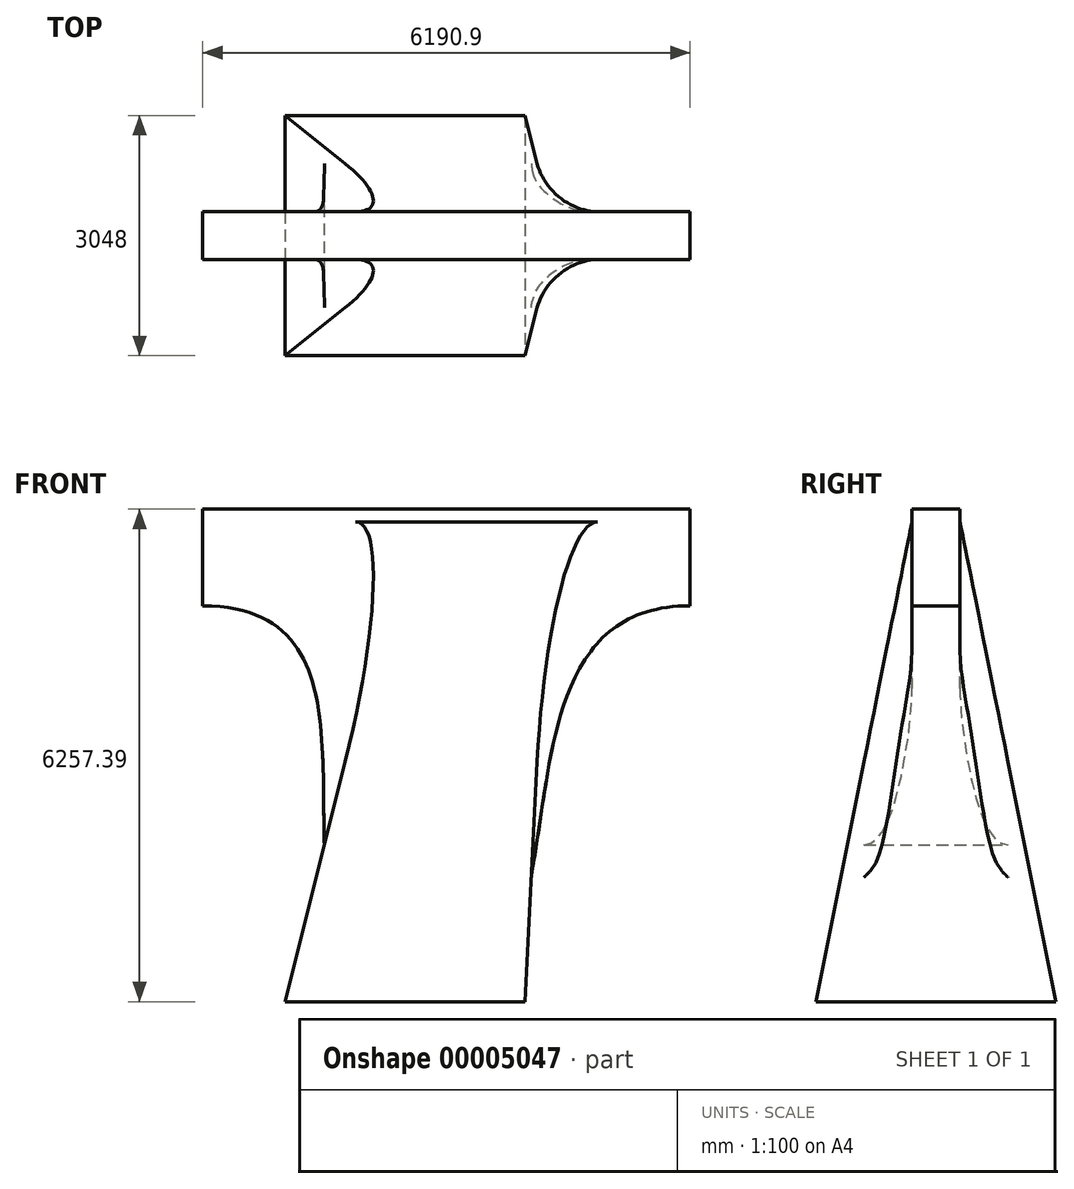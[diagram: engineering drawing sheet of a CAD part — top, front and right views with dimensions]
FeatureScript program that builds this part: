
annotation { "Feature Type Name" : "Feature", "Feature Type Description" : "" }
export const myFeature = defineFeature(function(context is Context, id is Id, definition is map)
    precondition{}
    {
        {
            var Q0;
            Q0=qCreatedBy(makeId("Top.planeOp"),FACE);
            cPlane(context, id + "F0", {"entities" : qUnion([Q0]), "cplaneType" : CPlaneType.OFFSET, "offset" : 6096 * mm, "width" : 152.4 * mm, "height" : 152.4 * mm});
        }
        {
            var Q0;
            Q0=qCreatedBy(makeId("Top.planeOp"),FACE);
            var sketch = newSketch(context, id + "F1", { "sketchPlane" : qUnion([Q0])});
            skLineSegment(sketch, "E0.bottom", {"start": v(-6096, 1524) * mm, "end": v(-3048, 1524) * mm});
            skLineSegment(sketch, "E0.top", {"start": v(-6096, -1524) * mm, "end": v(-3048, -1524) * mm});
            skLineSegment(sketch, "E0.left", {"start": v(-6096, 1524) * mm, "end": v(-6096, -1524) * mm});
            skLineSegment(sketch, "E0.right", {"start": v(-3048, 1524) * mm, "end": v(-3048, -1524) * mm});
            skSolve(sketch);
        }
        {
            var Q0;
            Q0=qCreatedBy(id+"F0.planeOp",FACE);
            var sketch = newSketch(context, id + "F2", { "sketchPlane" : qUnion([Q0])});
            skLineSegment(sketch, "E1.bottom", {"start": v(-4572, 304.8) * mm, "end": v(-2743.2, 304.8) * mm});
            skLineSegment(sketch, "E1.top", {"start": v(-4572, -304.8) * mm, "end": v(-2743.2, -304.8) * mm});
            skLineSegment(sketch, "E1.left", {"start": v(-4572, 304.8) * mm, "end": v(-4572, -304.8) * mm});
            skLineSegment(sketch, "E1.right", {"start": v(-2743.2, 304.8) * mm, "end": v(-2743.2, -304.8) * mm});
            skSolve(sketch);
        }
        {
            var Q0;
            Q0=makeQuery(id+"F1.imprint","IMPRINT",FACE,{"disambiguationData":[TD([[makeQuery(id+"F1.imprint","IMPRINT",EDGE,{"derivedFrom":sQuery(id+"F1.wireOp",EDGE,"E0.bottom")}),-1.0]])]});
            var Q1;
            Q1=makeQuery(id+"F2.imprint","IMPRINT",FACE,{"disambiguationData":[TD([[makeQuery(id+"F2.imprint","IMPRINT",EDGE,{"derivedFrom":sQuery(id+"F2.wireOp",EDGE,"E1.bottom")}),-1.0]])]});
            var Q2;
            Q2=sQuery(id+"F1.wireOp",VERTEX,"E0.right.end");
            var Q3;
            Q3=sQuery(id+"F2.wireOp",VERTEX,"E1.bottom.end");
            loft(context, id + "F3", {"sheetProfilesArray" : [{ "sheetProfileEntities" : qUnion([Q0]) }, { "sheetProfileEntities" : qUnion([Q1]) }], "connections" : [{ "connectionEntities" : qUnion([Q2, Q3]), "connectionEdgeQueries" : qUnion([]), "connectionEdgeParameters" : [] }]});
        }
        {
            var Q0;
            Q0=qCreatedBy(makeId("Front.planeOp"),FACE);
            var sketch = newSketch(context, id + "F4", { "sketchPlane" : qUnion([Q0])});
            skLineSegment(sketch, "E2", {"start": v(-7144.62, 6257.4) * mm, "end": v(-7144.62, 5029) * mm});
            skLineSegment(sketch, "E3", {"start": v(-7144.62, 6257.4) * mm, "end": v(-953.72, 6257.4) * mm});
            skLineSegment(sketch, "E4", {"start": v(-953.72, 6257.4) * mm, "end": v(-953.72, 5029) * mm});
            skFitSpline(sketch, "E5", {"points": [v(-953.72, 5029) * mm, v(-4320.53, 35.81) * mm], "startDerivative": vector(-8592.9, 0) * mm, "endDerivative": vector(-7049.9, 355.53) * mm});
            skFitSpline(sketch, "E6", {"points": [v(-7144.62, 5029) * mm, v(-4320.53, 35.81) * mm], "startDerivative": vector(8814.65, 0) * mm, "endDerivative": vector(7823.2, -629.46) * mm});
            skSolve(sketch);
        }
        {
            var Q0;
            Q0 = qSketchRegion(id + "F4", true);
            extrude(context, id + "F5", {"entities" : qUnion([Q0]), "operationType" : NewBodyOperationType.ADD, "endBound" : BoundingType.SYMMETRIC, "depth" : 609.6 * mm});
        }
        {
            var Q0;
            Q0=makeQuery(id+"F5.boolean.opBoolean","INTERSECT",EDGE,{"derivedFrom":[makeQuery(id+"F3.opLoft","SWEPT_FACE",FACE,{"disambiguationData":[OSD([sQuery(id+"F1.wireOp",EDGE,"E0.bottom"),sQuery(id+"F1.wireOp",EDGE,"E0.top"),sQuery(id+"F1.wireOp",EDGE,"E0.left"),sQuery(id+"F2.wireOp",EDGE,"E1.bottom"),sQuery(id+"F2.wireOp",EDGE,"E1.top"),sQuery(id+"F2.wireOp",EDGE,"E1.left")])]}),makeQuery(id+"F5.opExtrude","SWEPT_FACE",FACE,{"disambiguationData":[OSD([sQuery(id+"F4.wireOp",EDGE,"8ee350d9-5123-4934-8b01-f55df6ba07b4")])]})]});
            var Q1;
            Q1=makeQuery(id+"F5.boolean.opBoolean","INTERSECT",EDGE,{"derivedFrom":[makeQuery(id+"F3.opLoft","SWEPT_FACE",FACE,{"disambiguationData":[OSD([sQuery(id+"F1.wireOp",EDGE,"E0.bottom"),sQuery(id+"F1.wireOp",EDGE,"E0.top"),sQuery(id+"F1.wireOp",EDGE,"E0.left"),sQuery(id+"F2.wireOp",EDGE,"E1.bottom"),sQuery(id+"F2.wireOp",EDGE,"E1.top"),sQuery(id+"F2.wireOp",EDGE,"E1.left")])]}),makeQuery(id+"F5.opExtrude","CAP_FACE",FACE,{"disambiguationData":[OSD([sQuery(id+"F4.wireOp",EDGE,"E2"),sQuery(id+"F4.wireOp",EDGE,"E3"),sQuery(id+"F4.wireOp",EDGE,"E4"),sQuery(id+"F4.wireOp",EDGE,"E5"),sQuery(id+"F4.wireOp",EDGE,"8ee350d9-5123-4934-8b01-f55df6ba07b4")])],"isStart":false})]});
            var Q2;
            Q2=makeQuery(id+"F5.boolean.opBoolean","INTERSECT",EDGE,{"derivedFrom":[makeQuery(id+"F3.opLoft","SWEPT_FACE",FACE,{"disambiguationData":[OSD([sQuery(id+"F1.wireOp",EDGE,"E0.bottom"),sQuery(id+"F1.wireOp",EDGE,"E0.top"),sQuery(id+"F1.wireOp",EDGE,"E0.left"),sQuery(id+"F2.wireOp",EDGE,"E1.bottom"),sQuery(id+"F2.wireOp",EDGE,"E1.top"),sQuery(id+"F2.wireOp",EDGE,"E1.left")])]}),makeQuery(id+"F5.opExtrude","CAP_FACE",FACE,{"disambiguationData":[OSD([sQuery(id+"F4.wireOp",EDGE,"E2"),sQuery(id+"F4.wireOp",EDGE,"E3"),sQuery(id+"F4.wireOp",EDGE,"E4"),sQuery(id+"F4.wireOp",EDGE,"E5"),sQuery(id+"F4.wireOp",EDGE,"8ee350d9-5123-4934-8b01-f55df6ba07b4")])],"isStart":true})]});
            var Q3;
            Q3=makeQuery(id+"F5.boolean.opBoolean","INTERSECT",EDGE,{"derivedFrom":[makeQuery(id+"F3.opLoft","SWEPT_FACE",FACE,{"disambiguationData":[OSD([sQuery(id+"F1.wireOp",EDGE,"E0.bottom"),sQuery(id+"F1.wireOp",EDGE,"E0.top"),sQuery(id+"F1.wireOp",EDGE,"E0.right"),sQuery(id+"F2.wireOp",EDGE,"E1.bottom"),sQuery(id+"F2.wireOp",EDGE,"E1.top"),sQuery(id+"F2.wireOp",EDGE,"E1.right")])]}),makeQuery(id+"F5.opExtrude","CAP_FACE",FACE,{"disambiguationData":[OSD([sQuery(id+"F4.wireOp",EDGE,"E2"),sQuery(id+"F4.wireOp",EDGE,"E3"),sQuery(id+"F4.wireOp",EDGE,"E4"),sQuery(id+"F4.wireOp",EDGE,"E5"),sQuery(id+"F4.wireOp",EDGE,"8ee350d9-5123-4934-8b01-f55df6ba07b4")])],"isStart":false})]});
            var Q4;
            Q4=makeQuery(id+"F5.boolean.opBoolean","INTERSECT",EDGE,{"derivedFrom":[makeQuery(id+"F3.opLoft","SWEPT_FACE",FACE,{"disambiguationData":[OSD([sQuery(id+"F1.wireOp",EDGE,"E0.bottom"),sQuery(id+"F1.wireOp",EDGE,"E0.top"),sQuery(id+"F1.wireOp",EDGE,"E0.right"),sQuery(id+"F2.wireOp",EDGE,"E1.bottom"),sQuery(id+"F2.wireOp",EDGE,"E1.top"),sQuery(id+"F2.wireOp",EDGE,"E1.right")])]}),makeQuery(id+"F5.opExtrude","SWEPT_FACE",FACE,{"disambiguationData":[OSD([sQuery(id+"F4.wireOp",EDGE,"E5")])]})]});
            var Q5;
            Q5=makeQuery(id+"F5.boolean.opBoolean","INTERSECT",EDGE,{"derivedFrom":[makeQuery(id+"F3.opLoft","SWEPT_FACE",FACE,{"disambiguationData":[OSD([sQuery(id+"F1.wireOp",EDGE,"E0.bottom"),sQuery(id+"F1.wireOp",EDGE,"E0.top"),sQuery(id+"F1.wireOp",EDGE,"E0.right"),sQuery(id+"F2.wireOp",EDGE,"E1.bottom"),sQuery(id+"F2.wireOp",EDGE,"E1.top"),sQuery(id+"F2.wireOp",EDGE,"E1.right")])]}),makeQuery(id+"F5.opExtrude","CAP_FACE",FACE,{"disambiguationData":[OSD([sQuery(id+"F4.wireOp",EDGE,"E2"),sQuery(id+"F4.wireOp",EDGE,"E3"),sQuery(id+"F4.wireOp",EDGE,"E4"),sQuery(id+"F4.wireOp",EDGE,"E5"),sQuery(id+"F4.wireOp",EDGE,"8ee350d9-5123-4934-8b01-f55df6ba07b4")])],"isStart":true})]});
            fillet(context, id + "F6", {"entities" : qUnion([Q0, Q1, Q2, Q3, Q4, Q5]), "radius" : 609.6 * mm, "tangentPropagation" : true, "allowEdgeOverflow" : false});
        }
    });
